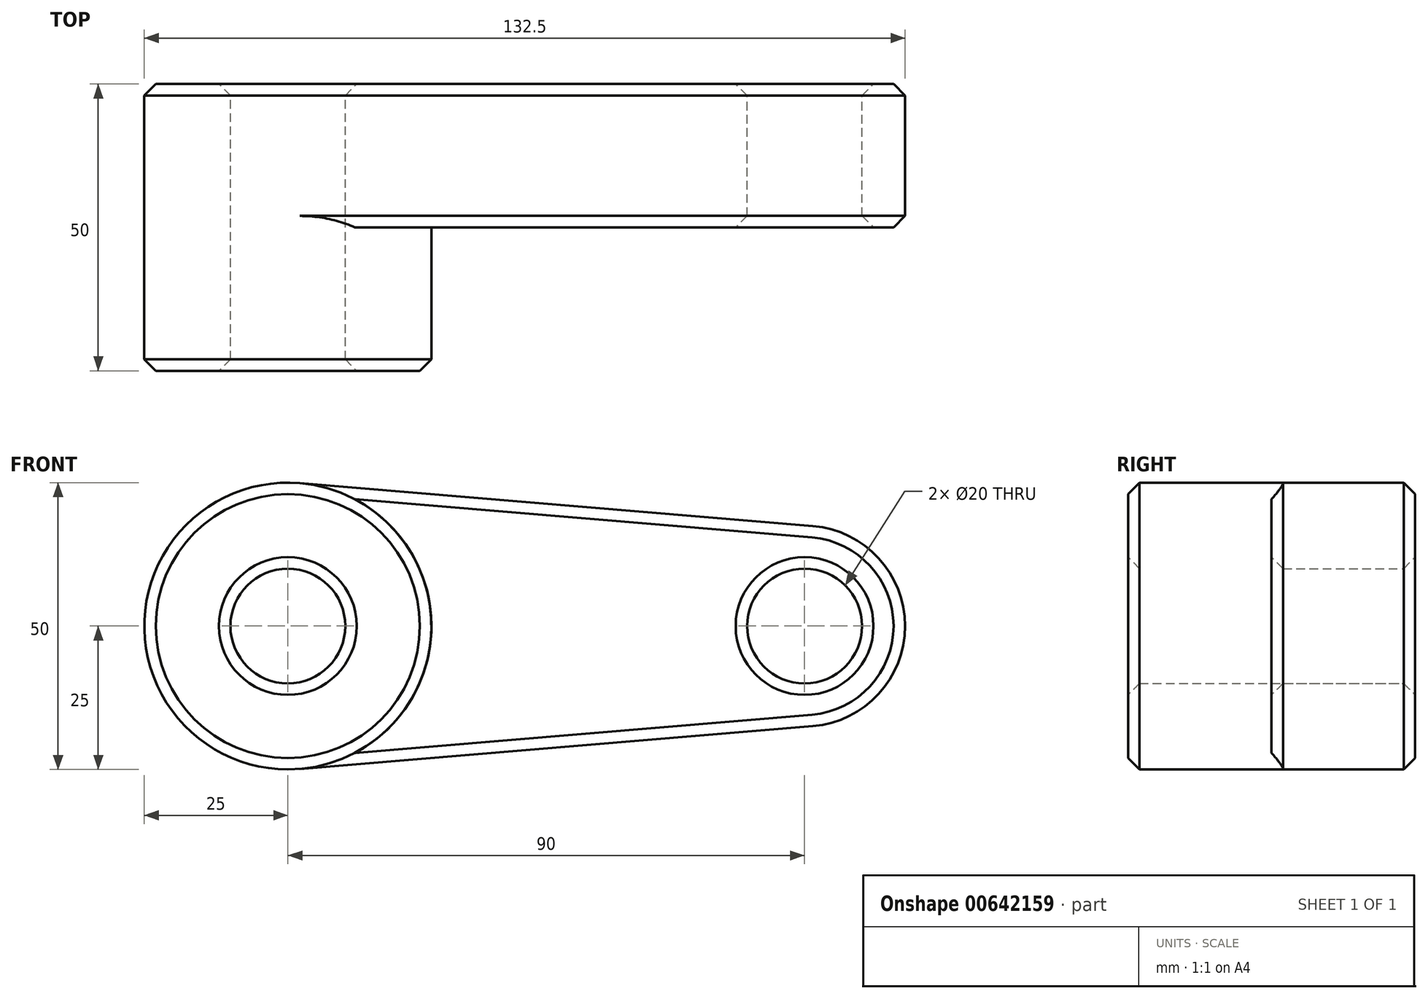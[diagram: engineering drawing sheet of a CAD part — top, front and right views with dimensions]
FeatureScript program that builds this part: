
annotation { "Feature Type Name" : "Feature", "Feature Type Description" : "" }
export const myFeature = defineFeature(function(context is Context, id is Id, definition is map)
    precondition{}
    {
        {
            var Q0;
            Q0=qCreatedBy(makeId("Front.planeOp"),FACE);
            var sketch = newSketch(context, id + "F0", { "sketchPlane" : qUnion([Q0])});
            skCircle(sketch, "E0", {"center": v(0, 0) * mm, "radius": 25 * mm});
            skCircle(sketch, "E1", {"center": v(90, 0) * mm, "radius": 17.5 * mm});
            skLineSegment(sketch, "E2", {"start": v(2.08, 24.91) * mm, "end": v(91.46, 17.44) * mm});
            skLineSegment(sketch, "E3", {"start": v(2.08, -24.91) * mm, "end": v(91.46, -17.44) * mm});
            skCircle(sketch, "E4", {"center": v(0, 0) * mm, "radius": 10 * mm});
            skCircle(sketch, "E5", {"center": v(90, 0) * mm, "radius": 10 * mm});
            skSolve(sketch);
        }
        {
            var Q0;
            Q0=qSketchRegion(id+"F0",true);
            extrude(context, id + "F1", {"entities" : qUnion([Q0]), "depth" : 25 * mm});
        }
        {
            var Q0;
            Q0=makeQuery(id+"F0.imprint","IMPRINT",FACE,{"disambiguationData":[TD([[makeQuery(id+"F0.imprint","IMPRINT",EDGE,{"derivedFrom":sQuery(id+"F0.wireOp",EDGE,"E4")}),-1.0]])]});
            extrude(context, id + "F2", {"entities" : qUnion([Q0]), "operationType" : NewBodyOperationType.ADD, "depth" : 50 * mm});
        }
        {
            var Q0;
            Q0=makeQuery(id+"F2.opExtrude","CAP_EDGE",EDGE,{"disambiguationData":[OSD([sQuery(id+"F0.wireOp",EDGE,"E0")])],"isStart":false});
            var Q1;
            Q1=makeQuery(id+"F2.opExtrude","CAP_EDGE",EDGE,{"disambiguationData":[OSD([sQuery(id+"F0.wireOp",EDGE,"E4")])],"isStart":false});
            var Q2;
            Q2=makeQuery(id+"F1.opExtrude","CAP_EDGE",EDGE,{"disambiguationData":[OSD([sQuery(id+"F0.wireOp",EDGE,"E5")])],"isStart":false});
            chamfer(context, id + "F3", {"entities" : qUnion([Q0, Q1, Q2]), "width" : 2 * mm, "tangentPropagation" : true});
        }
        {
            var Q0;
            Q0=makeQuery(id+"F1.opExtrude","SWEPT_FACE",FACE,{"disambiguationData":[OSD([sQuery(id+"F0.wireOp",EDGE,"E1")])]});
            var Q1;
            Q1=makeQuery(id+"F1.opExtrude","CAP_EDGE",EDGE,{"disambiguationData":[OSD([sQuery(id+"F0.wireOp",EDGE,"E5")])],"isStart":true});
            var Q2;
            Q2=makeQuery(id+"F1.opExtrude","CAP_EDGE",EDGE,{"disambiguationData":[OSD([sQuery(id+"F0.wireOp",EDGE,"E4")])],"isStart":true});
            chamfer(context, id + "F4", {"entities" : qUnion([Q0, Q1, Q2]), "width" : 2 * mm, "tangentPropagation" : true});
        }
    });
